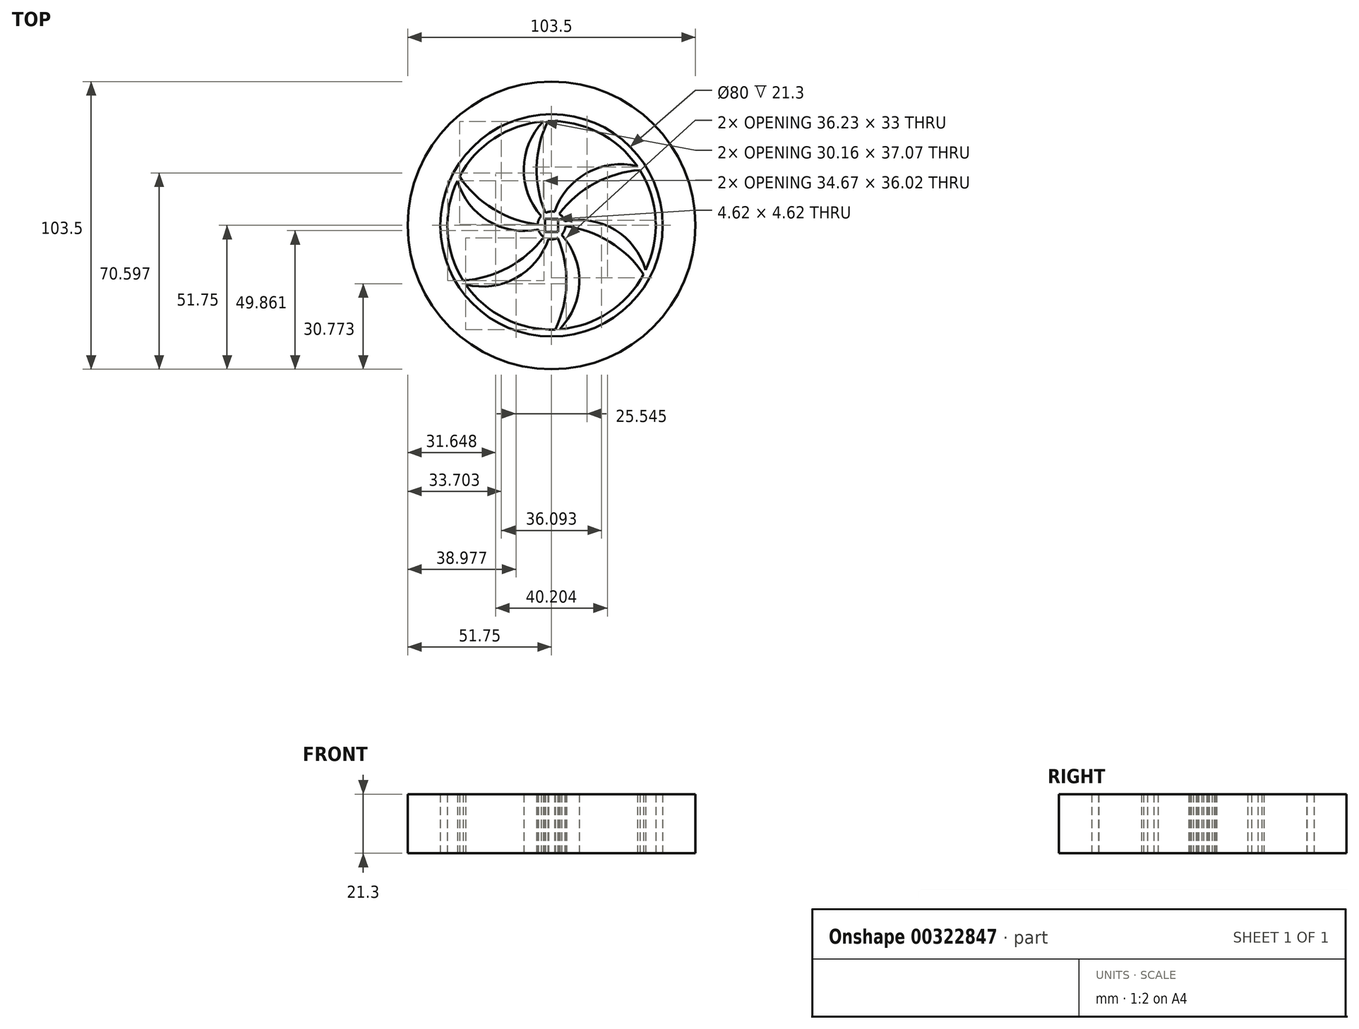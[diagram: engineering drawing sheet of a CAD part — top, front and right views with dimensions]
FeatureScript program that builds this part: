
annotation { "Feature Type Name" : "Feature", "Feature Type Description" : "" }
export const myFeature = defineFeature(function(context is Context, id is Id, definition is map)
    precondition{}
    {
        {
            var Q0;
            Q0=qCreatedBy(makeId("Top.planeOp"),FACE);
            var sketch = newSketch(context, id + "F0", { "sketchPlane" : qUnion([Q0])});
            skCircle(sketch, "E0", {"center": v(0, 0) * mm, "radius": 51.75 * mm});
            skCircle(sketch, "E1", {"center": v(0, 0) * mm, "radius": 40 * mm});
            skSolve(sketch);
        }
        {
            var Q0;
            Q0=qSketchRegion(id+"F0",true);
            extrude(context, id + "F1", {"entities" : qUnion([Q0]), "depth" : 21.3 * mm});
        }
        {
            var Q0;
            Q0=qCreatedBy(makeId("Top.planeOp"),FACE);
            var sketch = newSketch(context, id + "F2", { "sketchPlane" : qUnion([Q0])});
            skCircle(sketch, "E2", {"center": v(0, 0) * mm, "radius": 40 * mm});
            skCircle(sketch, "E3.cCircle", {"center": v(0, 0) * mm, "radius": 40 * mm, "construction": true});
            skLineSegment(sketch, "E3.3", {"start": v(0, -40) * mm, "end": v(-34.64, -20) * mm});
            skArc(sketch, "E4", {"start": v(-34.64, 20) * mm, "mid": v(-24.42, 2.7) * mm, "end": v(-4.77, -1.5) * mm});
            skArc(sketch, "E5", {"start": v(-34.64, 20) * mm, "mid": v(-22.13, 6.68) * mm, "end": v(-5, 0.31) * mm});
            skArc(sketch, "E6.1.0", {"start": v(-34.64, -20) * mm, "mid": v(-16.85, -15.82) * mm, "end": v(-2.77, -4.17) * mm});
            skArc(sketch, "E6.1.1", {"start": v(-34.64, -20) * mm, "mid": v(-14.55, -19.8) * mm, "end": v(-1.1, -4.88) * mm});
            skArc(sketch, "E6.2.0", {"start": v(0, -40) * mm, "mid": v(5.28, -22.5) * mm, "end": v(2.22, -4.48) * mm});
            skArc(sketch, "E6.2.1", {"start": v(0, -40) * mm, "mid": v(9.87, -22.5) * mm, "end": v(3.68, -3.38) * mm});
            skArc(sketch, "E6.3.0", {"start": v(34.64, -20) * mm, "mid": v(22.13, -6.68) * mm, "end": v(5, -0.31) * mm});
            skArc(sketch, "E6.3.1", {"start": v(34.64, -20) * mm, "mid": v(24.42, -2.7) * mm, "end": v(4.77, 1.5) * mm});
            skArc(sketch, "E6.4.0", {"start": v(34.64, 20) * mm, "mid": v(16.85, 15.82) * mm, "end": v(2.77, 4.17) * mm});
            skArc(sketch, "E6.4.1", {"start": v(34.64, 20) * mm, "mid": v(14.55, 19.8) * mm, "end": v(1.1, 4.88) * mm});
            skArc(sketch, "E6.5.0", {"start": v(0, 40) * mm, "mid": v(-5.28, 22.5) * mm, "end": v(-2.22, 4.48) * mm});
            skArc(sketch, "E6.5.1", {"start": v(0, 40) * mm, "mid": v(-9.87, 22.5) * mm, "end": v(-3.68, 3.38) * mm});
            skCircle(sketch, "E7", {"center": v(0, 0) * mm, "radius": 37.5 * mm});
            skCircle(sketch, "E8", {"center": v(0, 0) * mm, "radius": 5 * mm});
            skLineSegment(sketch, "E9.bottom", {"start": v(2.31, -2.31) * mm, "end": v(-2.31, -2.31) * mm});
            skLineSegment(sketch, "E9.top", {"start": v(2.31, 2.31) * mm, "end": v(-2.31, 2.3) * mm});
            skLineSegment(sketch, "E9.left", {"start": v(2.31, -2.3) * mm, "end": v(2.31, 2.31) * mm});
            skLineSegment(sketch, "E9.right", {"start": v(-2.31, -2.31) * mm, "end": v(-2.31, 2.3) * mm});
            skSolve(sketch);
        }
        {
            var Q0;
            Q0=qSketchRegion(id+"F2",true);
            var Q1;
            {var subQ0=sQuery(id+"F2.wireOp",EDGE,"E8");var subQ1=sQuery(id+"F2.wireOp",EDGE,"E4");var subQ2=makeQuery(id+"F2.imprint","INTERSECT",VERTEX,{"derivedFrom":[subQ1,subQ0]});Q1=makeQuery(id+"F2.imprint","IMPRINT",FACE,{"disambiguationData":[TD([[makeQuery(id+"F2.imprint","IMPRINT",EDGE,{"disambiguationData":[TD([[subQ2,1.0]])],"derivedFrom":subQ1}),1.0]])]});}
            var Q2;
            {var subQ0=sQuery(id+"F2.wireOp",EDGE,"E8");var subQ1=sQuery(id+"F2.wireOp",EDGE,"E6.5.0");var subQ2=makeQuery(id+"F2.imprint","INTERSECT",VERTEX,{"derivedFrom":[subQ1,subQ0]});Q2=makeQuery(id+"F2.imprint","IMPRINT",FACE,{"disambiguationData":[TD([[makeQuery(id+"F2.imprint","IMPRINT",EDGE,{"disambiguationData":[TD([[subQ2,1.0]])],"derivedFrom":subQ1}),-1.0]])]});}
            var Q3;
            {var subQ0=sQuery(id+"F2.wireOp",EDGE,"E8");var subQ1=sQuery(id+"F2.wireOp",EDGE,"E6.4.0");var subQ2=makeQuery(id+"F2.imprint","INTERSECT",VERTEX,{"derivedFrom":[subQ1,subQ0]});Q3=makeQuery(id+"F2.imprint","IMPRINT",FACE,{"disambiguationData":[TD([[makeQuery(id+"F2.imprint","IMPRINT",EDGE,{"disambiguationData":[TD([[subQ2,1.0]])],"derivedFrom":subQ1}),-1.0]])]});}
            var Q4;
            Q4=makeQuery(id+"F2.imprint","IMPRINT",FACE,{"disambiguationData":[TD([[makeQuery(id+"F2.imprint","IMPRINT",EDGE,{"derivedFrom":sQuery(id+"F2.wireOp",EDGE,"E9.bottom")}),1.0]])]});
            var Q5;
            {var subQ0=sQuery(id+"F2.wireOp",EDGE,"E8");var subQ1=sQuery(id+"F2.wireOp",EDGE,"E6.3.0");var subQ2=makeQuery(id+"F2.imprint","INTERSECT",VERTEX,{"derivedFrom":[subQ1,subQ0]});Q5=makeQuery(id+"F2.imprint","IMPRINT",FACE,{"disambiguationData":[TD([[makeQuery(id+"F2.imprint","IMPRINT",EDGE,{"disambiguationData":[TD([[subQ2,1.0]])],"derivedFrom":subQ1}),-1.0]])]});}
            var Q6;
            {var subQ0=sQuery(id+"F2.wireOp",EDGE,"E8");var subQ1=sQuery(id+"F2.wireOp",EDGE,"E6.1.0");var subQ2=makeQuery(id+"F2.imprint","INTERSECT",VERTEX,{"derivedFrom":[subQ1,subQ0]});Q6=makeQuery(id+"F2.imprint","IMPRINT",FACE,{"disambiguationData":[TD([[makeQuery(id+"F2.imprint","IMPRINT",EDGE,{"disambiguationData":[TD([[subQ2,1.0]])],"derivedFrom":subQ1}),-1.0]])]});}
            var Q7;
            {var subQ0=sQuery(id+"F2.wireOp",EDGE,"E8");var subQ1=sQuery(id+"F2.wireOp",EDGE,"E6.2.0");var subQ2=makeQuery(id+"F2.imprint","INTERSECT",VERTEX,{"derivedFrom":[subQ1,subQ0]});Q7=makeQuery(id+"F2.imprint","IMPRINT",FACE,{"disambiguationData":[TD([[makeQuery(id+"F2.imprint","IMPRINT",EDGE,{"disambiguationData":[TD([[subQ2,1.0]])],"derivedFrom":subQ1}),-1.0]])]});}
            extrude(context, id + "F3", {"entities" : qUnion([Q0, Q1, Q2, Q3, Q4, Q5, Q6, Q7]), "depth" : 21.3 * mm});
        }
    });
